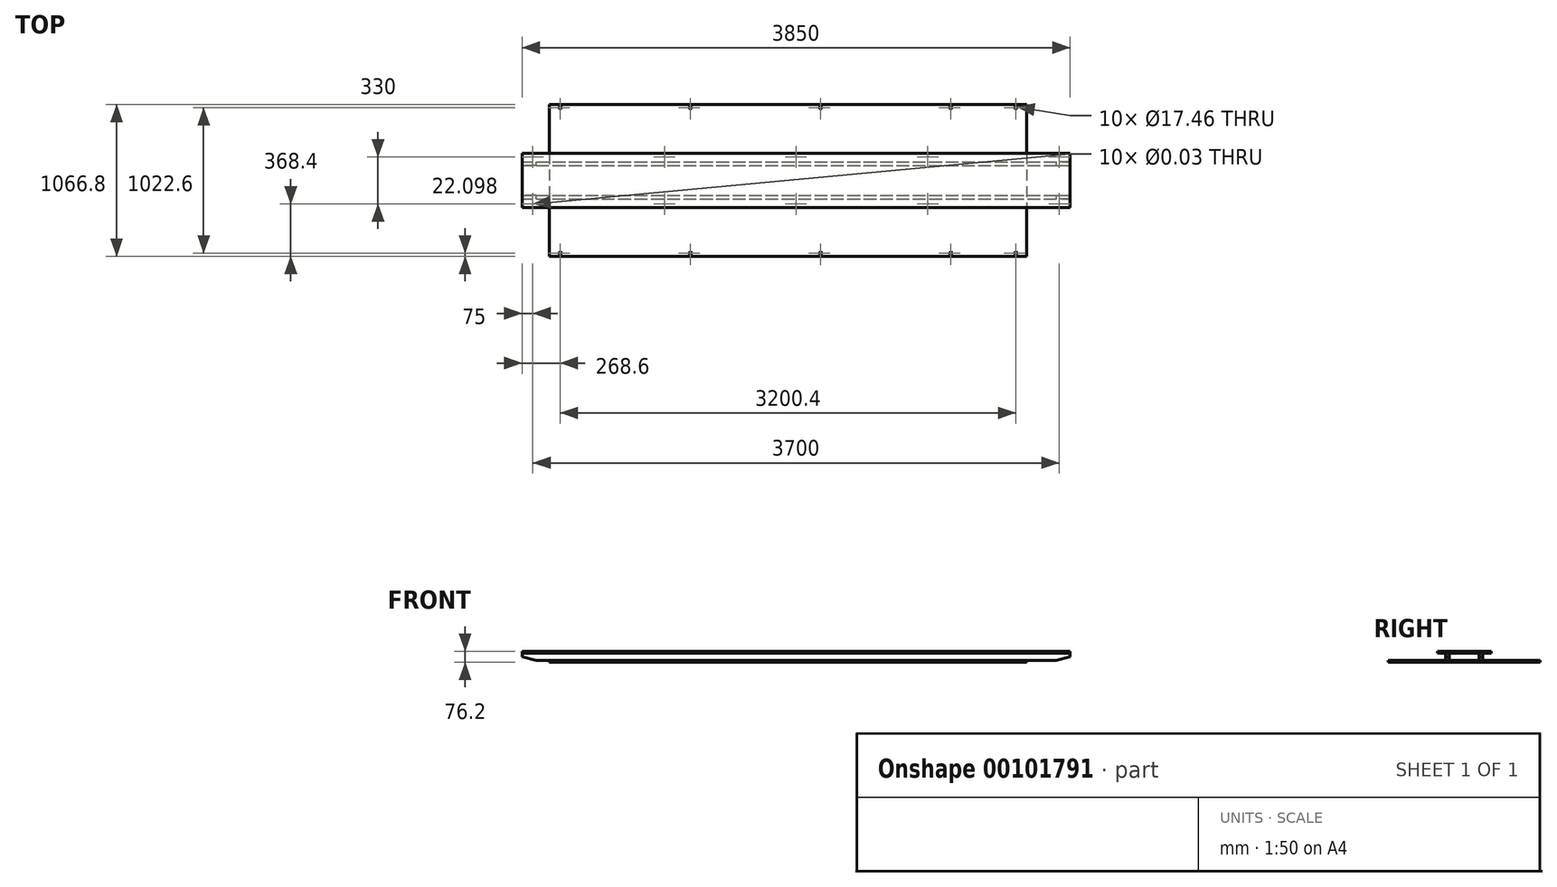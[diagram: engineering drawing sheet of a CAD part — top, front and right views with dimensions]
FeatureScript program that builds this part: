
annotation { "Feature Type Name" : "Feature", "Feature Type Description" : "" }
export const myFeature = defineFeature(function(context is Context, id is Id, definition is map)
    precondition{}
    {
        {
            var Q0;
            Q0=qCreatedBy(makeId("Top.planeOp"),FACE);
            var sketch = newSketch(context, id + "F0", { "sketchPlane" : qUnion([Q0])});
            skLineSegment(sketch, "E0.bottom", {"start": v(-1676.4, 533.4) * mm, "end": v(1676.4, 533.4) * mm});
            skLineSegment(sketch, "E0.top", {"start": v(-1676.4, -533.4) * mm, "end": v(1676.4, -533.4) * mm});
            skLineSegment(sketch, "E0.left", {"start": v(-1676.4, 533.4) * mm, "end": v(-1676.4, -533.4) * mm});
            skLineSegment(sketch, "E0.right", {"start": v(1676.4, 533.4) * mm, "end": v(1676.4, -533.4) * mm});
            skPoint(sketch, "E0.middle", {"position": v(0, 0) * mm});
            skLineSegment(sketch, "E1.0", {"start": v(1600.2, 533.4) * mm, "end": v(1600.2, -533.4) * mm, "construction": true});
            skLineSegment(sketch, "E2.0", {"start": v(1143, 533.4) * mm, "end": v(1143, -533.4) * mm, "construction": true});
            skLineSegment(sketch, "E3.0", {"start": v(228.6, 533.4) * mm, "end": v(228.6, -533.4) * mm, "construction": true});
            skLineSegment(sketch, "E4.0", {"start": v(-685.8, 533.4) * mm, "end": v(-685.8, -533.4) * mm, "construction": true});
            skLineSegment(sketch, "E5.0", {"start": v(-1600.2, 533.4) * mm, "end": v(-1600.2, -533.4) * mm, "construction": true});
            skLineSegment(sketch, "E6", {"start": v(-1744.77, 0) * mm, "end": v(1824.44, 0) * mm, "construction": true});
            skLineSegment(sketch, "E7.0", {"start": v(-1744.77, 511.3) * mm, "end": v(1824.44, 511.3) * mm, "construction": true});
            skLineSegment(sketch, "E8.MirrorCS", {"start": v(-1744.77, -511.3) * mm, "end": v(1824.44, -511.3) * mm, "construction": true});
            skPoint(sketch, "E9", {"position": v(-1600.2, 511.3) * mm});
            skPoint(sketch, "E10", {"position": v(-685.8, 511.3) * mm});
            skPoint(sketch, "E11", {"position": v(228.6, 511.3) * mm});
            skPoint(sketch, "E12", {"position": v(1143, 511.3) * mm});
            skPoint(sketch, "E13", {"position": v(1600.2, 511.3) * mm});
            skPoint(sketch, "E14", {"position": v(1600.2, -511.3) * mm});
            skPoint(sketch, "E15", {"position": v(1143, -511.3) * mm});
            skPoint(sketch, "E16", {"position": v(228.6, -511.3) * mm});
            skPoint(sketch, "E17", {"position": v(-685.8, -511.3) * mm});
            skPoint(sketch, "E18", {"position": v(-1600.2, -511.3) * mm});
            skSolve(sketch);
        }
        {
            var Q0;
            Q0=makeQuery(id+"F0.imprint","IMPRINT",FACE,{"disambiguationData":[TD([[makeQuery(id+"F0.imprint","IMPRINT",EDGE,{"derivedFrom":sQuery(id+"F0.wireOp",EDGE,"E0.bottom")}),-1.0]])]});
            extrude(context, id + "F1", {"entities" : qUnion([Q0]), "depth" : 12.7 * mm});
        }
        {
            var Q0;
            Q0=sQuery(id+"F0.wireOp",VERTEX,"E9");
            var Q1;
            Q1=sQuery(id+"F0.wireOp",VERTEX,"E10");
            var Q2;
            Q2=sQuery(id+"F0.wireOp",VERTEX,"E11");
            var Q3;
            Q3=sQuery(id+"F0.wireOp",VERTEX,"E12");
            var Q4;
            Q4=sQuery(id+"F0.wireOp",VERTEX,"E13");
            var Q5;
            Q5=sQuery(id+"F0.wireOp",VERTEX,"E14");
            var Q6;
            Q6=sQuery(id+"F0.wireOp",VERTEX,"E15");
            var Q7;
            Q7=sQuery(id+"F0.wireOp",VERTEX,"E16");
            var Q8;
            Q8=sQuery(id+"F0.wireOp",VERTEX,"E17");
            var Q9;
            Q9=sQuery(id+"F0.wireOp",VERTEX,"E18");
            var Q10;
            Q10=makeQuery(id+"F1.opExtrude","SWEPT_BODY",BODY,{"disambiguationData":[OSD([sQuery(id+"F0.wireOp",EDGE,"E0.bottom"),sQuery(id+"F0.wireOp",EDGE,"E0.top"),sQuery(id+"F0.wireOp",EDGE,"E0.left"),sQuery(id+"F0.wireOp",EDGE,"E0.right")])]});
            hole(context, id + "F2", {"style" : HoleStyle.SIMPLE, "endStyle" : HoleEndStyle.BLIND, "oppositeDirection" : true, "holeDiameter" : 17.46 * mm, "holeDepth" : 50.8 * mm, "locations" : qUnion([Q0, Q1, Q2, Q3, Q4, Q5, Q6, Q7, Q8, Q9]), "scope" : qUnion([Q10])});
        }
        {
            var Q0;
            Q0=makeQuery(id+"F1.opExtrude","CAP_FACE",FACE,{"disambiguationData":[OSD([sQuery(id+"F0.wireOp",EDGE,"E0.bottom"),sQuery(id+"F0.wireOp",EDGE,"E0.top"),sQuery(id+"F0.wireOp",EDGE,"E0.left"),sQuery(id+"F0.wireOp",EDGE,"E0.right")])],"isStart":false});
            cPlane(context, id + "F3", {"entities" : qUnion([Q0]), "cplaneType" : CPlaneType.OFFSET, "offset" : 63.5 * mm, "width" : 152.4 * mm, "height" : 152.4 * mm});
        }
        {
            var Q0;
            Q0=qCreatedBy(id+"F3.planeOp",FACE);
            var sketch = newSketch(context, id + "F4", { "sketchPlane" : qUnion([Q0])});
            skLineSegment(sketch, "E19", {"start": v(0, 937.47) * mm, "end": v(0, -1122.85) * mm, "construction": true});
            skLineSegment(sketch, "E20.0", {"start": v(1981.2, 937.47) * mm, "end": v(1981.2, -1122.85) * mm, "construction": true});
            skLineSegment(sketch, "E21", {"start": v(-1966.75, 0) * mm, "end": v(2855.28, 0) * mm, "construction": true});
            skLineSegment(sketch, "E22.0", {"start": v(-1966.75, 190) * mm, "end": v(2855.28, 190) * mm, "construction": true});
            skLineSegment(sketch, "E23.bottom", {"start": v(1981.2, 190) * mm, "end": v(-1868.8, 190) * mm});
            skLineSegment(sketch, "E23.top", {"start": v(1981.2, -190) * mm, "end": v(-1868.8, -190) * mm});
            skLineSegment(sketch, "E23.left", {"start": v(1981.2, 190) * mm, "end": v(1981.2, -190) * mm});
            skLineSegment(sketch, "E23.right", {"start": v(-1868.8, 190) * mm, "end": v(-1868.8, -190) * mm});
            skSolve(sketch);
        }
        {
            var Q0;
            Q0 = qSketchRegion(id + "F4", true);
            extrude(context, id + "F5", {"entities" : qUnion([Q0]), "oppositeDirection" : true, "depth" : 12.7 * mm});
        }
        {
            var Q0;
            Q0=makeQuery(id+"F5.opExtrude","CAP_FACE",FACE,{"disambiguationData":[OSD([sQuery(id+"F4.wireOp",EDGE,"E23.bottom"),sQuery(id+"F4.wireOp",EDGE,"E23.top"),sQuery(id+"F4.wireOp",EDGE,"E23.left"),sQuery(id+"F4.wireOp",EDGE,"E23.right")])],"isStart":true});
            var sketch = newSketch(context, id + "F6", { "sketchPlane" : qUnion([Q0])});
            skLineSegment(sketch, "E24.0", {"start": v(-1868.8, 190) * mm, "end": v(-1868.8, -190) * mm, "construction": true});
            skLineSegment(sketch, "E25", {"start": v(-2024.4, 0) * mm, "end": v(2568.54, 0) * mm, "construction": true});
            skLineSegment(sketch, "E26.0", {"start": v(-1793.8, 190) * mm, "end": v(-1793.8, -190) * mm, "construction": true});
            skLineSegment(sketch, "E27.0", {"start": v(-868.8, 190) * mm, "end": v(-868.8, -190) * mm, "construction": true});
            skLineSegment(sketch, "E28.0", {"start": v(56.2, 190) * mm, "end": v(56.2, -190) * mm, "construction": true});
            skLineSegment(sketch, "E29.0", {"start": v(981.2, 190) * mm, "end": v(981.2, -190) * mm, "construction": true});
            skLineSegment(sketch, "E30.0", {"start": v(1906.2, 190) * mm, "end": v(1906.2, -190) * mm, "construction": true});
            skLineSegment(sketch, "E31.0", {"start": v(-2024.4, 165) * mm, "end": v(2568.54, 165) * mm, "construction": true});
            skLineSegment(sketch, "E32.0", {"start": v(-2024.4, -165) * mm, "end": v(2568.54, -165) * mm, "construction": true});
            skPoint(sketch, "E33", {"position": v(1906.2, 165) * mm});
            skPoint(sketch, "E34", {"position": v(1906.2, -165) * mm});
            skPoint(sketch, "E35", {"position": v(981.2, -165) * mm});
            skPoint(sketch, "E36", {"position": v(981.2, 165) * mm});
            skPoint(sketch, "E37", {"position": v(56.2, 165) * mm});
            skPoint(sketch, "E38", {"position": v(56.2, -165) * mm});
            skPoint(sketch, "E39", {"position": v(-868.8, -165) * mm});
            skPoint(sketch, "E40", {"position": v(-868.8, 165) * mm});
            skPoint(sketch, "E41", {"position": v(-1793.8, 165) * mm});
            skPoint(sketch, "E42", {"position": v(-1793.8, -165) * mm});
            skSolve(sketch);
        }
        {
            var Q0;
            Q0=sQuery(id+"F6.wireOp",VERTEX,"E41");
            var Q1;
            Q1=sQuery(id+"F6.wireOp",VERTEX,"E42");
            var Q2;
            Q2=sQuery(id+"F6.wireOp",VERTEX,"E40");
            var Q3;
            Q3=sQuery(id+"F6.wireOp",VERTEX,"E39");
            var Q4;
            Q4=sQuery(id+"F6.wireOp",VERTEX,"E37");
            var Q5;
            Q5=sQuery(id+"F6.wireOp",VERTEX,"E36");
            var Q6;
            Q6=sQuery(id+"F6.wireOp",VERTEX,"E38");
            var Q7;
            Q7=sQuery(id+"F6.wireOp",VERTEX,"E35");
            var Q8;
            Q8=sQuery(id+"F6.wireOp",VERTEX,"E33");
            var Q9;
            Q9=sQuery(id+"F6.wireOp",VERTEX,"E34");
            var Q10;
            Q10=makeQuery(id+"F5.opExtrude","SWEPT_BODY",BODY,{"disambiguationData":[OSD([sQuery(id+"F4.wireOp",EDGE,"E23.bottom"),sQuery(id+"F4.wireOp",EDGE,"E23.top"),sQuery(id+"F4.wireOp",EDGE,"E23.left"),sQuery(id+"F4.wireOp",EDGE,"E23.right")])]});
            hole(context, id + "F7", {"style" : HoleStyle.SIMPLE, "endStyle" : HoleEndStyle.THROUGH, "standardTappedOrClearance" : lookupTablePath({ "standard" : "ANSI", "size" : "11/16 (0.69)", "type" : "Drilled" }), "standardBlindInLast" : lookupTablePath({ "standard" : "ANSI", "size" : "11/16", "type" : "Drilled" }), "holeDiameter" : 11 / 406.4 * mm, "locations" : qUnion([Q0, Q1, Q2, Q3, Q4, Q5, Q6, Q7, Q8, Q9]), "scope" : qUnion([Q10]), "isTappedThrough" : true});
        }
        {
            var Q0;
            Q0=makeQuery(id+"F5.opExtrude","SWEPT_FACE",FACE,{"disambiguationData":[OSD([sQuery(id+"F4.wireOp",EDGE,"E23.left")])]});
            var sketch = newSketch(context, id + "F8", { "sketchPlane" : qUnion([Q0])});
            skLineSegment(sketch, "E43.0", {"start": v(190, 63.5) * mm, "end": v(-190, 63.5) * mm, "construction": true});
            skLineSegment(sketch, "E44.0", {"start": v(533.4, 12.7) * mm, "end": v(-533.4, 12.7) * mm, "construction": true});
            skLineSegment(sketch, "E45", {"start": v(0, 182.6) * mm, "end": v(0, -95.9) * mm, "construction": true});
            skLineSegment(sketch, "E46.0", {"start": v(-130, 182.6) * mm, "end": v(-130, -95.9) * mm, "construction": true});
            skLineSegment(sketch, "E47.bottom", {"start": v(-130, 63.5) * mm, "end": v(-104.6, 63.5) * mm});
            skLineSegment(sketch, "E47.top", {"start": v(-130, 12.7) * mm, "end": v(-104.6, 12.7) * mm});
            skLineSegment(sketch, "E47.left", {"start": v(-130, 63.5) * mm, "end": v(-130, 12.7) * mm});
            skLineSegment(sketch, "E47.right", {"start": v(-104.6, 63.5) * mm, "end": v(-104.6, 12.7) * mm});
            skLineSegment(sketch, "E48.MirrorCS", {"start": v(130, 12.7) * mm, "end": v(104.6, 12.7) * mm});
            skLineSegment(sketch, "E49.MirrorCS", {"start": v(130, 63.5) * mm, "end": v(104.6, 63.5) * mm});
            skLineSegment(sketch, "E50.MirrorCS", {"start": v(130, 63.5) * mm, "end": v(130, 12.7) * mm});
            skLineSegment(sketch, "E51.MirrorCS", {"start": v(104.6, 63.5) * mm, "end": v(104.6, 12.7) * mm});
            skSolve(sketch);
        }
        {
            var Q0;
            Q0 = qSketchRegion(id + "F8", true);
            extrude(context, id + "F9", {"entities" : qUnion([Q0]), "oppositeDirection" : true, "depth" : 3850 * mm});
        }
        {
            var Q0;
            Q0=makeQuery(id+"F9.opExtrude","CAP_EDGE",EDGE,{"disambiguationData":[OSD([sQuery(id+"F8.wireOp",EDGE,"E48.MirrorCS")])],"isStart":false});
            chamfer(context, id + "F10", {"entities" : qUnion([Q0]), "chamferType" : ChamferType.TWO_OFFSETS, "width1" : 25 * mm, "oppositeDirection" : false, "width2" : 100 * mm, "tangentPropagation" : true});
        }
        {
            var Q0;
            Q0=makeQuery(id+"F9.opExtrude","CAP_EDGE",EDGE,{"disambiguationData":[OSD([sQuery(id+"F8.wireOp",EDGE,"E47.top")])],"isStart":false});
            chamfer(context, id + "F11", {"entities" : qUnion([Q0]), "chamferType" : ChamferType.TWO_OFFSETS, "width1" : 25 * mm, "oppositeDirection" : true, "width2" : 100 * mm, "tangentPropagation" : true});
        }
        {
            var Q0;
            Q0=makeQuery(id+"F9.opExtrude","CAP_EDGE",EDGE,{"disambiguationData":[OSD([sQuery(id+"F8.wireOp",EDGE,"E48.MirrorCS")])],"isStart":true});
            chamfer(context, id + "F12", {"entities" : qUnion([Q0]), "chamferType" : ChamferType.TWO_OFFSETS, "width1" : 25 * mm, "oppositeDirection" : true, "width2" : 100 * mm, "tangentPropagation" : true});
        }
        {
            var Q0;
            Q0=makeQuery(id+"F9.opExtrude","CAP_EDGE",EDGE,{"disambiguationData":[OSD([sQuery(id+"F8.wireOp",EDGE,"E47.top")])],"isStart":true});
            chamfer(context, id + "F13", {"entities" : qUnion([Q0]), "chamferType" : ChamferType.TWO_OFFSETS, "width1" : 25 * mm, "oppositeDirection" : false, "width2" : 100 * mm, "tangentPropagation" : true});
        }
    });
